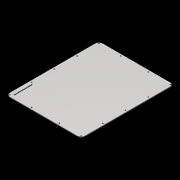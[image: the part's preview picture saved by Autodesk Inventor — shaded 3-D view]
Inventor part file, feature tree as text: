
AUTODESK INVENTOR PART (.ipt)
format: ipt  version: 2018.2 (Build 222227000, 227)  size: 143,872 bytes
history: native  units: mm
features: other x4, extrude x4, sketch x4, reference x1
ambient origin geometry x8: Origin, YZ Plane, XZ Plane, XY Plane, X Axis, Y Axis, Z Axis, Center Point
bodies: Body1 (feature_tree)
feature tree (13):
  other  "ソリッド1"
  extrude  "押し出し1"  Depth=380.0mm
  extrude  "押し出し2"  Depth=470.0mm
  extrude  "押し出し3"  Depth=4.5mm
  extrude  "押し出し4"  Depth=10.0mm
  sketch  "スケッチ1"
  sketch  "スケッチ2"
  sketch  "スケッチ3"
  reference  "参照1"
  sketch  "スケッチ4"
  other  "<userpath>\Documents\CAD\eatx_case\layout.iam"
  other  "layout.iam"
  other  "backpanel:1"
